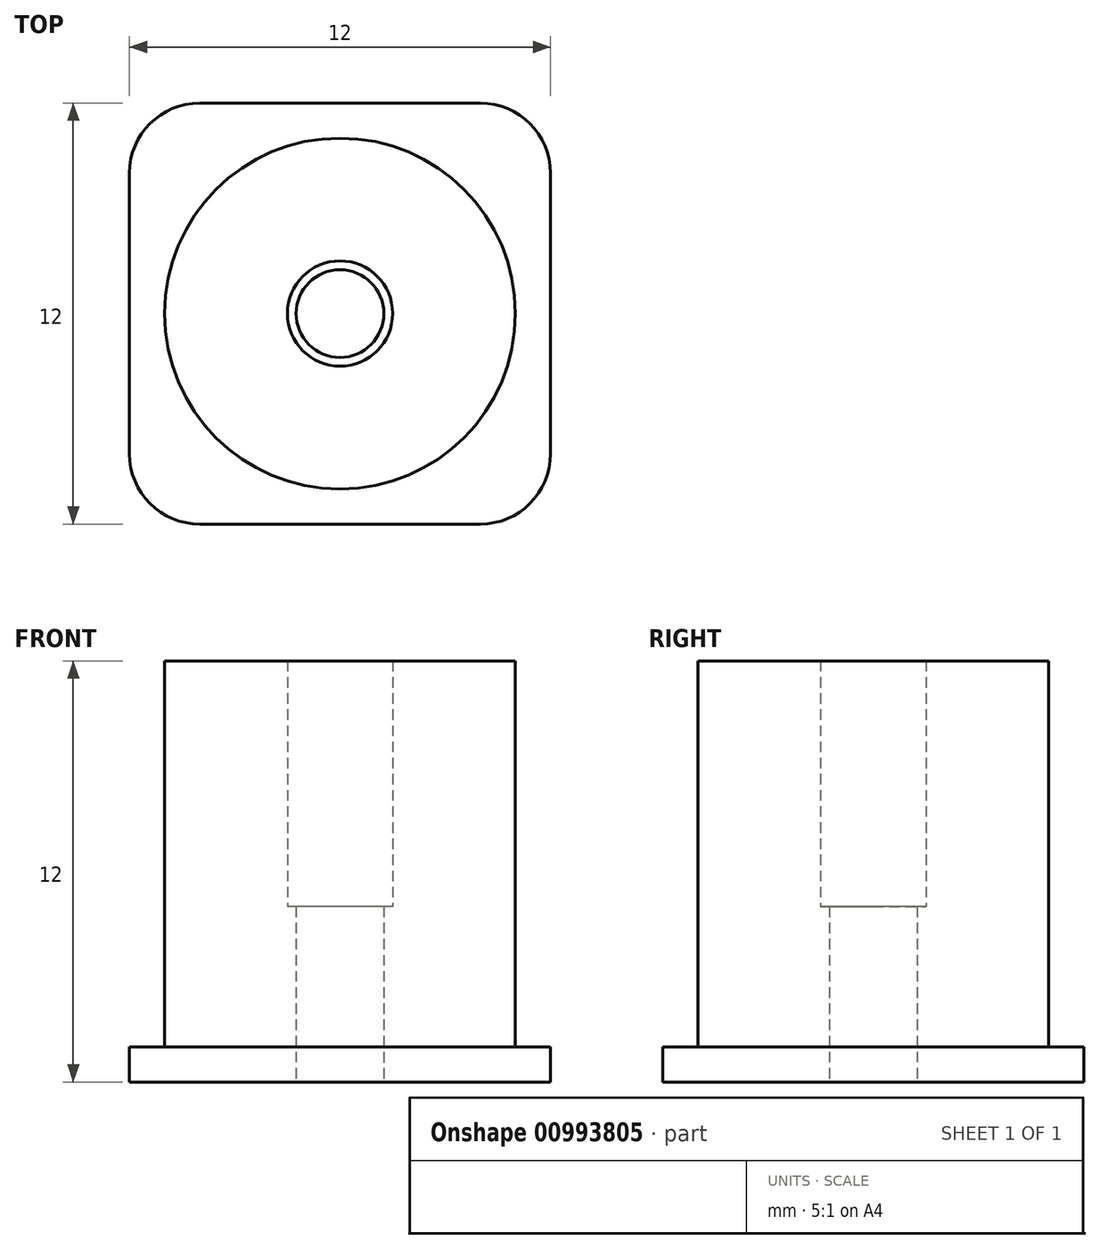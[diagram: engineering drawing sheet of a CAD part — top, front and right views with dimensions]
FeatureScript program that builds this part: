
annotation { "Feature Type Name" : "Feature", "Feature Type Description" : "" }
export const myFeature = defineFeature(function(context is Context, id is Id, definition is map)
    precondition{}
    {
        {
            var Q0;
            Q0=qCreatedBy(makeId("Top.planeOp"),FACE);
            var sketch = newSketch(context, id + "F0", { "sketchPlane" : qUnion([Q0])});
            skCircle(sketch, "E0", {"center": v(0, 0) * mm, "radius": 5 * mm});
            skCircle(sketch, "E1", {"center": v(0, 0) * mm, "radius": 1.5 * mm});
            skLineSegment(sketch, "E2.bottom", {"start": v(6, 6) * mm, "end": v(-6, 6) * mm});
            skLineSegment(sketch, "E2.top", {"start": v(6, -6) * mm, "end": v(-6, -6) * mm});
            skLineSegment(sketch, "E2.left", {"start": v(6, 6) * mm, "end": v(6, -6) * mm});
            skLineSegment(sketch, "E2.right", {"start": v(-6, 6) * mm, "end": v(-6, -6) * mm});
            skCircle(sketch, "E3", {"center": v(0, 0) * mm, "radius": 1.25 * mm});
            skSolve(sketch);
        }
        {
            var Q0;
            Q0=makeQuery(id+"F0.imprint","IMPRINT",FACE,{"disambiguationData":[TD([[makeQuery(id+"F0.imprint","IMPRINT",EDGE,{"derivedFrom":sQuery(id+"F0.wireOp",EDGE,"E0")}),1.0]])]});
            extrude(context, id + "F1", {"entities" : qUnion([Q0]), "depth" : 12 * mm, "offsetDistance" : 25 * mm});
        }
        {
            var Q0;
            Q0=makeQuery(id+"F0.imprint","IMPRINT",FACE,{"disambiguationData":[TD([[makeQuery(id+"F0.imprint","IMPRINT",EDGE,{"derivedFrom":sQuery(id+"F0.wireOp",EDGE,"E1")}),1.0]])]});
            extrude(context, id + "F2", {"entities" : qUnion([Q0]), "operationType" : NewBodyOperationType.ADD, "depth" : 5 * mm, "offsetDistance" : 25 * mm});
        }
        {
            var Q0;
            Q0=makeQuery(id+"F0.imprint","IMPRINT",FACE,{"disambiguationData":[TD([[makeQuery(id+"F0.imprint","IMPRINT",EDGE,{"derivedFrom":sQuery(id+"F0.wireOp",EDGE,"E0")}),-1.0]])]});
            extrude(context, id + "F3", {"entities" : qUnion([Q0]), "operationType" : NewBodyOperationType.ADD, "depth" : 1 * mm, "offsetDistance" : 25 * mm});
        }
        {
            var Q0;
            Q0=makeQuery(id+"F3.opExtrude","SWEPT_EDGE",EDGE,{"disambiguationData":[OSD([sQuery(id+"F0.wireOp",EDGE,"E2.top"),sQuery(id+"F0.wireOp",EDGE,"E2.right")])]});
            var Q1;
            Q1=makeQuery(id+"F3.opExtrude","SWEPT_EDGE",EDGE,{"disambiguationData":[OSD([sQuery(id+"F0.wireOp",EDGE,"E2.bottom"),sQuery(id+"F0.wireOp",EDGE,"E2.right")])]});
            var Q2;
            Q2=makeQuery(id+"F3.opExtrude","SWEPT_EDGE",EDGE,{"disambiguationData":[OSD([sQuery(id+"F0.wireOp",EDGE,"E2.top"),sQuery(id+"F0.wireOp",EDGE,"E2.left")])]});
            var Q3;
            Q3=makeQuery(id+"F3.opExtrude","SWEPT_EDGE",EDGE,{"disambiguationData":[OSD([sQuery(id+"F0.wireOp",EDGE,"E2.bottom"),sQuery(id+"F0.wireOp",EDGE,"E2.left")])]});
            fillet(context, id + "F4", {"entities" : qUnion([Q0, Q1, Q2, Q3]), "tangentPropagation" : true, "radius" : 2 * mm, "defaultsChanged" : true, "vertexSettings" : [], "allowEdgeOverflow" : false});
        }
    });
